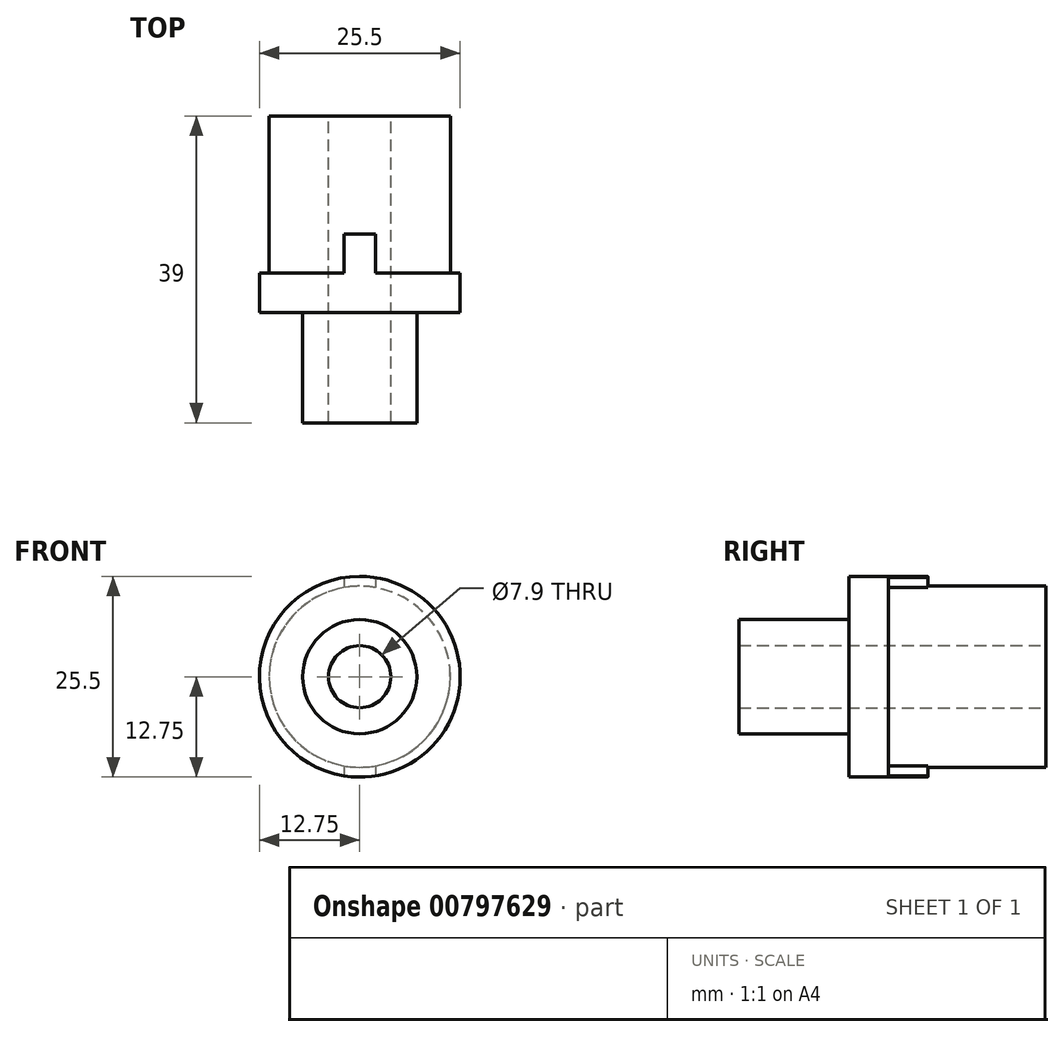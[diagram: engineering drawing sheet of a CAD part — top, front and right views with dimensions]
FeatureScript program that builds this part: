
annotation { "Feature Type Name" : "Feature", "Feature Type Description" : "" }
export const myFeature = defineFeature(function(context is Context, id is Id, definition is map)
    precondition{}
    {
        {
            var Q0;
            Q0=qCreatedBy(makeId("Front.planeOp"),FACE);
            var sketch = newSketch(context, id + "F0", { "sketchPlane" : qUnion([Q0])});
            skCircle(sketch, "E0", {"center": v(0, 0) * mm, "radius": 7.25 * mm});
            skSolve(sketch);
        }
        {
            var Q0;
            Q0=makeQuery(id+"F0.imprint","IMPRINT",FACE,{"disambiguationData":[TD([[makeQuery(id+"F0.imprint","IMPRINT",EDGE,{"derivedFrom":sQuery(id+"F0.wireOp",EDGE,"E0")}),1.0]])]});
            extrude(context, id + "F1", {"entities" : qUnion([Q0]), "depth" : 14 * mm, "offsetDistance" : 25 * mm});
        }
        {
            var Q0;
            Q0=makeQuery(id+"F1.opExtrude","CAP_FACE",FACE,{"disambiguationData":[OSD([sQuery(id+"F0.wireOp",EDGE,"E0")])],"isStart":true});
            var sketch = newSketch(context, id + "F2", { "sketchPlane" : qUnion([Q0])});
            skCircle(sketch, "E1", {"center": v(0, 0) * mm, "radius": 9.25 * mm});
            skCircle(sketch, "E2", {"center": v(0, 0) * mm, "radius": 11.25 * mm});
            skSolve(sketch);
        }
        {
            var Q0;
            Q0=makeQuery(id+"F1.opExtrude","CAP_FACE",FACE,{"disambiguationData":[OSD([sQuery(id+"F0.wireOp",EDGE,"E0")])],"isStart":false});
            var sketch = newSketch(context, id + "F3", { "sketchPlane" : qUnion([Q0])});
            skCircle(sketch, "E3", {"center": v(0, 0) * mm, "radius": 3 * mm});
            skSolve(sketch);
        }
        {
            var Q0;
            Q0=makeQuery(id+"F3.imprint","IMPRINT",FACE,{"disambiguationData":[TD([[makeQuery(id+"F3.imprint","IMPRINT",EDGE,{"derivedFrom":sQuery(id+"F3.wireOp",EDGE,"E3")}),1.0]])]});
            extrude(context, id + "F4", {"entities" : qUnion([Q0]), "operationType" : NewBodyOperationType.REMOVE, "endBound" : BoundingType.THROUGH_ALL, "oppositeDirection" : true, "depth" : 25 * mm, "offsetDistance" : 25 * mm});
        }
        {
            var Q0;
            Q0=makeQuery(id+"F2.imprint","IMPRINT",FACE,{"disambiguationData":[TD([[makeQuery(id+"F2.imprint","IMPRINT",EDGE,{"derivedFrom":sQuery(id+"F2.wireOp",EDGE,"E1")}),1.0]])]});
            cPlane(context, id + "F5", {"entities" : qUnion([Q0]), "cplaneType" : CPlaneType.OFFSET, "offset" : 0 * mm, "width" : 150 * mm, "height" : 150 * mm});
        }
        {
            var Q0;
            Q0=qCreatedBy(id+"F5.planeOp",FACE);
            var sketch = newSketch(context, id + "F6", { "sketchPlane" : qUnion([Q0])});
            skCircle(sketch, "E4", {"center": v(0, 0) * mm, "radius": 12.75 * mm});
            skSolve(sketch);
        }
        {
            var Q0;
            Q0=qSketchRegion(id+"F6",true);
            extrude(context, id + "F7", {"entities" : qUnion([Q0]), "operationType" : NewBodyOperationType.ADD, "depth" : 25 * mm, "offsetDistance" : 25 * mm});
        }
        {
            var Q0;
            Q0=makeQuery(id+"F7.opExtrude","CAP_FACE",FACE,{"disambiguationData":[OSD([sQuery(id+"F6.wireOp",EDGE,"E4")])],"isStart":false});
            var sketch = newSketch(context, id + "F8", { "sketchPlane" : qUnion([Q0])});
            skCircle(sketch, "E5", {"center": v(0, 0) * mm, "radius": 3.95 * mm});
            skSolve(sketch);
        }
        {
            var Q0;
            Q0=makeQuery(id+"F8.imprint","IMPRINT",FACE,{"disambiguationData":[TD([[makeQuery(id+"F8.imprint","IMPRINT",EDGE,{"derivedFrom":sQuery(id+"F8.wireOp",EDGE,"E5")}),1.0]])]});
            extrude(context, id + "F9", {"entities" : qUnion([Q0]), "operationType" : NewBodyOperationType.REMOVE, "endBound" : BoundingType.THROUGH_ALL, "oppositeDirection" : true, "depth" : 25 * mm, "offsetDistance" : 25 * mm});
        }
        {
            var Q0;
            Q0=makeQuery(id+"F7.opExtrude","CAP_FACE",FACE,{"disambiguationData":[OSD([sQuery(id+"F6.wireOp",EDGE,"E4")])],"isStart":false});
            var sketch = newSketch(context, id + "F10", { "sketchPlane" : qUnion([Q0])});
            skCircle(sketch, "E6", {"center": v(0, 0) * mm, "radius": 11.5 * mm});
            skSolve(sketch);
        }
        {
            var Q0;
            Q0=makeQuery(id+"F10.imprint","IMPRINT",FACE,{"disambiguationData":[TD([[makeQuery(id+"F10.imprint","IMPRINT",EDGE,{"derivedFrom":sQuery(id+"F10.wireOp",EDGE,"E6")}),-1.0]])]});
            extrude(context, id + "F11", {"entities" : qUnion([Q0]), "operationType" : NewBodyOperationType.REMOVE, "oppositeDirection" : true, "depth" : 20 * mm, "offsetDistance" : 25 * mm});
        }
        {
            var Q0;
            Q0=makeQuery(id+"F11.boolean.opBoolean","COPY",FACE,{"derivedFrom":makeQuery(id+"F11.opExtrude","CAP_FACE",FACE,{"disambiguationData":[OSD([sQuery(id+"F6.wireOp",EDGE,"E4"),sQuery(id+"F10.wireOp",EDGE,"E6")])],"isStart":false})});
            var sketch = newSketch(context, id + "F12", { "sketchPlane" : qUnion([Q0])});
            skLineSegment(sketch, "E7", {"start": v(0, 13.66) * mm, "end": v(0, -14.8) * mm, "construction": true});
            skLineSegment(sketch, "E8", {"start": v(-2, 12.6) * mm, "end": v(-2, 11.32) * mm});
            skLineSegment(sketch, "E9", {"start": v(2, 12.6) * mm, "end": v(2, 11.32) * mm});
            skLineSegment(sketch, "E10", {"start": v(-14.5, 0) * mm, "end": v(13.95, 0) * mm, "construction": true});
            skLineSegment(sketch, "E11.MirrorCS", {"start": v(-6, 12.6) * mm, "end": v(-6, 11.32) * mm});
            skLineSegment(sketch, "E12.MirrorCS", {"start": v(10.5, 0) * mm, "end": v(-17.95, 0) * mm, "construction": true});
            skLineSegment(sketch, "E13", {"start": v(-2, -11.32) * mm, "end": v(-2, -12.6) * mm});
            skLineSegment(sketch, "E14", {"start": v(2, -11.32) * mm, "end": v(2, -12.6) * mm});
            skPoint(sketch, "E15.MirrorCS.end.orphan", {"position": v(-6, 11.32) * mm});
            skPoint(sketch, "E15.MirrorCS.start.orphan", {"position": v(-6, 12.6) * mm});
            skSolve(sketch);
        }
        {
            var Q0;
            {var subQ0=sQuery(id+"F12.wireOp",EDGE,"E8");Q0=makeQuery(id+"F12.imprint","IMPRINT",FACE,{"disambiguationData":[TD([[makeQuery(id+"F12.imprint","IMPRINT",EDGE,{"derivedFrom":subQ0}),1.0]])]});}
            var Q1;
            {var subQ0=sQuery(id+"F12.wireOp",EDGE,"E13");Q1=makeQuery(id+"F12.imprint","IMPRINT",FACE,{"disambiguationData":[TD([[makeQuery(id+"F12.imprint","IMPRINT",EDGE,{"derivedFrom":subQ0}),1.0]])]});}
            extrude(context, id + "F13", {"entities" : qUnion([Q0, Q1]), "operationType" : NewBodyOperationType.ADD, "depth" : 5 * mm, "offsetDistance" : 25 * mm});
        }
    });
